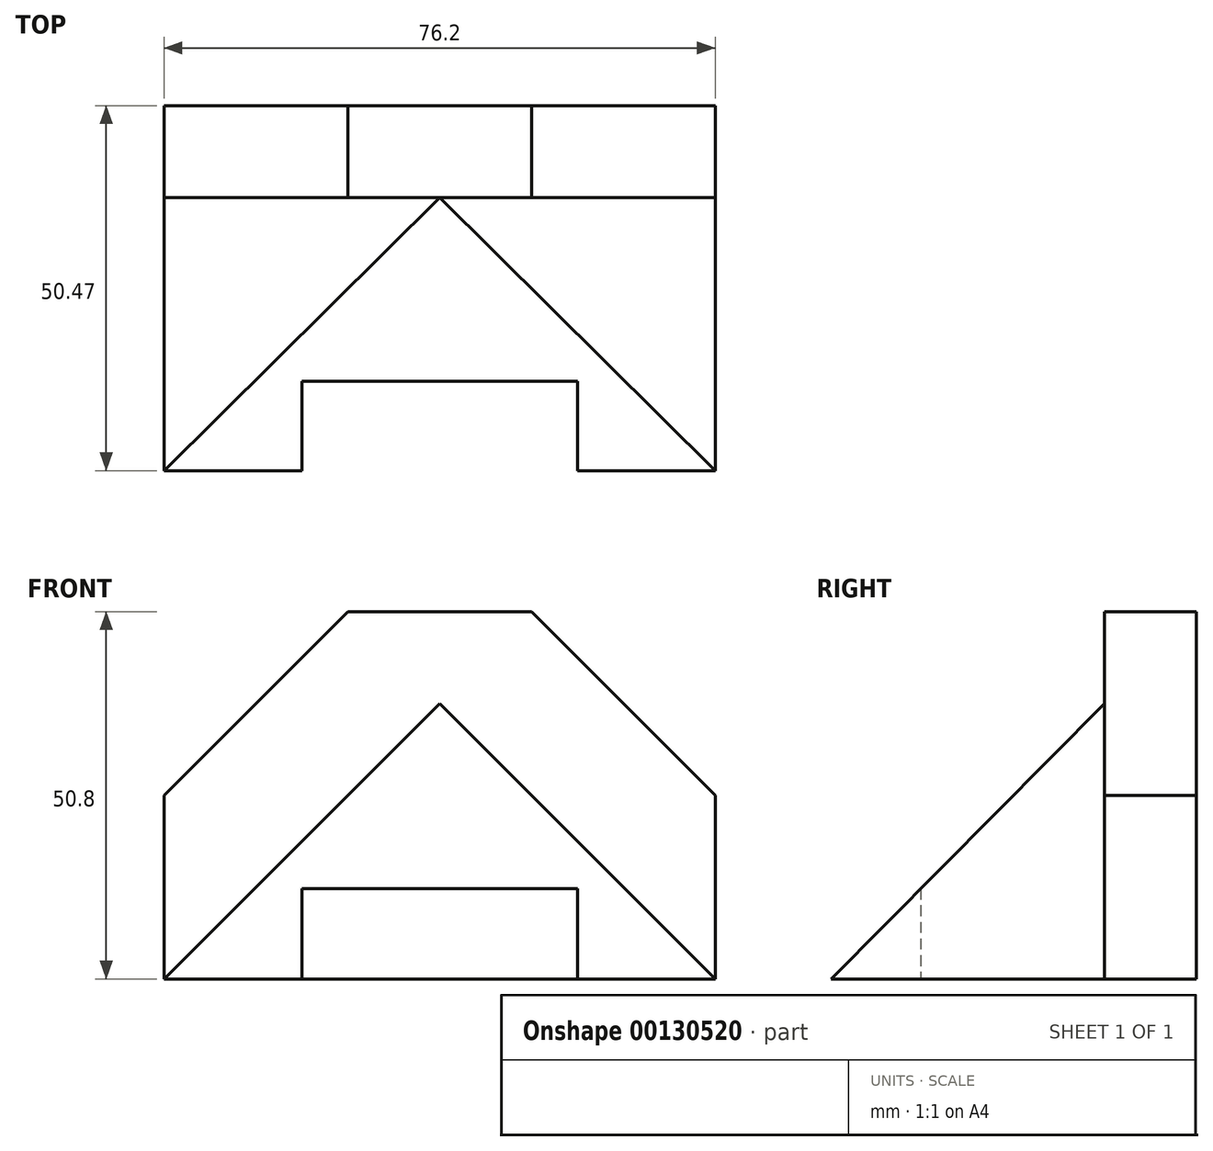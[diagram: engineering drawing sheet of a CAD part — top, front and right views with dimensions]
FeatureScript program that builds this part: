
annotation { "Feature Type Name" : "Feature", "Feature Type Description" : "" }
export const myFeature = defineFeature(function(context is Context, id is Id, definition is map)
    precondition{}
    {
        {
            var Q0;
            Q0=qCreatedBy(makeId("Front.planeOp"),FACE);
            var sketch = newSketch(context, id + "F0", { "sketchPlane" : qUnion([Q0])});
            skLineSegment(sketch, "E0", {"start": v(0, 25.4) * mm, "end": v(0, 0) * mm});
            skLineSegment(sketch, "E1", {"start": v(0, 0) * mm, "end": v(76.2, 0) * mm});
            skLineSegment(sketch, "E2", {"start": v(76.2, 0) * mm, "end": v(76.2, 25.4) * mm});
            skLineSegment(sketch, "E3", {"start": v(76.2, 25.4) * mm, "end": v(50.8, 50.8) * mm});
            skLineSegment(sketch, "E4", {"start": v(50.8, 50.8) * mm, "end": v(25.4, 50.8) * mm});
            skLineSegment(sketch, "E5", {"start": v(25.4, 50.8) * mm, "end": v(0, 25.4) * mm});
            skLineSegment(sketch, "E6", {"start": v(25.4, 50.8) * mm, "end": v(0, 50.8) * mm, "construction": true});
            skPoint(sketch, "E6.endSnap0", {"position": v(0, 12.7) * mm});
            skLineSegment(sketch, "E7", {"start": v(0, 50.8) * mm, "end": v(0, 25.4) * mm, "construction": true});
            skSolve(sketch);
        }
        {
            var Q0;
            Q0 = qSketchRegion(id + "F0", true);
            extrude(context, id + "F1", {"entities" : qUnion([Q0]), "depth" : 12.7 * mm});
        }
        {
            var Q0;
            Q0=makeQuery(id+"F1.opExtrude","CAP_FACE",FACE,{"disambiguationData":[OSD([sQuery(id+"F0.wireOp",EDGE,"E0"),sQuery(id+"F0.wireOp",EDGE,"E1"),sQuery(id+"F0.wireOp",EDGE,"E2"),sQuery(id+"F0.wireOp",EDGE,"E3"),sQuery(id+"F0.wireOp",EDGE,"E4"),sQuery(id+"F0.wireOp",EDGE,"E5")])],"isStart":false});
            var sketch = newSketch(context, id + "F2", { "sketchPlane" : qUnion([Q0])});
            skLineSegment(sketch, "E8", {"start": v(76.2, 0) * mm, "end": v(0, 0) * mm});
            skLineSegment(sketch, "E9", {"start": v(0, 0) * mm, "end": v(38.1, 38.1) * mm});
            skLineSegment(sketch, "E10", {"start": v(38.1, 38.1) * mm, "end": v(76.2, 0) * mm});
            skSolve(sketch);
        }
        {
            var Q0;
            Q0 = qSketchRegion(id + "F2", true);
            extrude(context, id + "F3", {"entities" : qUnion([Q0]), "operationType" : NewBodyOperationType.ADD, "depth" : 38.1 * mm});
        }
        {
            var Q0;
            Q0=makeQuery(id+"F3.boolean.opBoolean","MERGE",FACE,{"derivedFrom":[makeQuery(id+"F1.opExtrude","SWEPT_FACE",FACE,{"disambiguationData":[OSD([sQuery(id+"F0.wireOp",EDGE,"E1")])]}),makeQuery(id+"F3.opExtrude","SWEPT_FACE",FACE,{"disambiguationData":[OSD([sQuery(id+"F2.wireOp",EDGE,"E8")])]})]});
            var sketch = newSketch(context, id + "F4", { "sketchPlane" : qUnion([Q0])});
            skLineSegment(sketch, "E11", {"start": v(57.15, 50.8) * mm, "end": v(57.15, 38.1) * mm});
            skLineSegment(sketch, "E12", {"start": v(57.15, 38.1) * mm, "end": v(19.05, 38.1) * mm});
            skLineSegment(sketch, "E13", {"start": v(19.05, 38.1) * mm, "end": v(19.05, 50.8) * mm});
            skLineSegment(sketch, "E14", {"start": v(19.05, 50.8) * mm, "end": v(57.15, 50.8) * mm});
            skSolve(sketch);
        }
        {
            var Q0;
            Q0 = qSketchRegion(id + "F4", true);
            extrude(context, id + "F5", {"entities" : qUnion([Q0]), "operationType" : NewBodyOperationType.REMOVE, "endBound" : BoundingType.THROUGH_ALL, "oppositeDirection" : true, "depth" : 25.4 * mm});
        }
        {
            var Q0;
            Q0=makeQuery(id+"F1.opExtrude","SWEPT_FACE",FACE,{"disambiguationData":[OSD([sQuery(id+"F0.wireOp",EDGE,"E2")])]});
            var sketch = newSketch(context, id + "F6", { "sketchPlane" : qUnion([Q0])});
            skLineSegment(sketch, "E15", {"start": v(0, 0) * mm, "end": v(0, 38.1) * mm, "construction": true});
            skLineSegment(sketch, "E16", {"start": v(0, 38.1) * mm, "end": v(-12.7, 38.1) * mm, "construction": true});
            skLineSegment(sketch, "E17", {"start": v(-12.7, 38.1) * mm, "end": v(-51.2, -0.73) * mm});
            skLineSegment(sketch, "E18", {"start": v(-51.2, -0.73) * mm, "end": v(-51.2, 38.1) * mm});
            skLineSegment(sketch, "E19", {"start": v(-51.2, 38.1) * mm, "end": v(-12.7, 38.1) * mm});
            skSolve(sketch);
        }
        {
            var Q0;
            Q0 = qSketchRegion(id + "F6", true);
            extrude(context, id + "F7", {"entities" : qUnion([Q0]), "operationType" : NewBodyOperationType.REMOVE, "endBound" : BoundingType.THROUGH_ALL, "oppositeDirection" : true, "depth" : 25.4 * mm});
        }
    });
